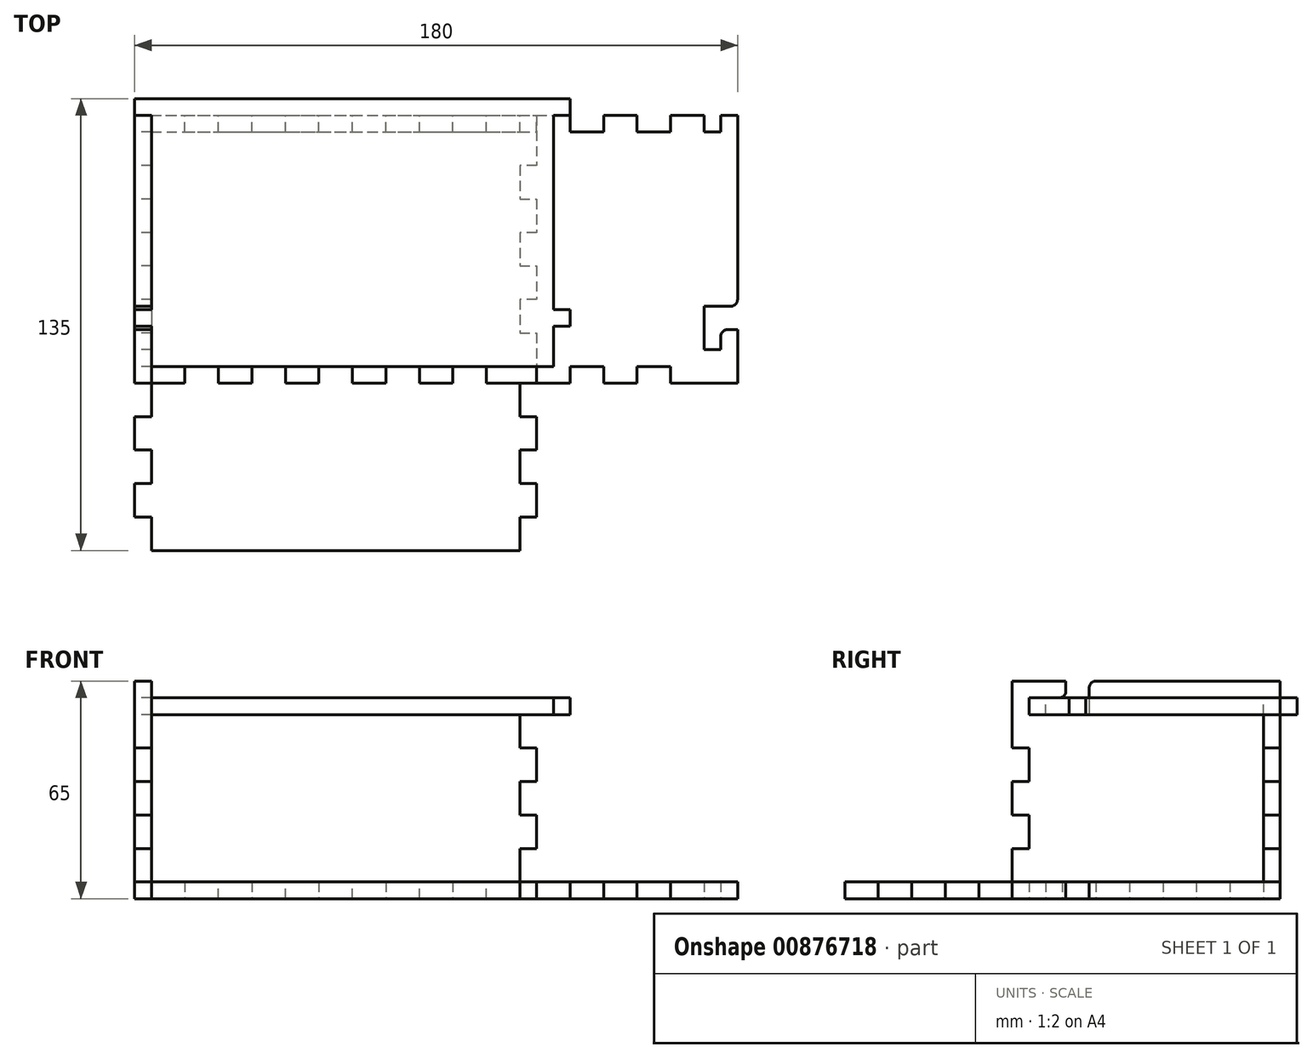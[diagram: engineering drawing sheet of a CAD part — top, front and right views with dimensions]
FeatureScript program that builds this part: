
annotation { "Feature Type Name" : "Feature", "Feature Type Description" : "" }
export const myFeature = defineFeature(function(context is Context, id is Id, definition is map)
    precondition{}
    {
        {
            assignVariable(context, id + "F0", {"name" : "thick", "anyValue" : 5});
        }
        {
            var Q0;
            Q0=qCreatedBy(makeId("Top.planeOp"),FACE);
            var sketch = newSketch(context, id + "F1", { "sketchPlane" : qUnion([Q0])});
            skLineSegment(sketch, "E0", {"start": v(0, 60.97) * mm, "end": v(0, 0) * mm, "construction": true});
            skLineSegment(sketch, "E1", {"start": v(0, 0) * mm, "end": v(112.46, 0) * mm, "construction": true});
            skPoint(sketch, "E2", {"position": v(65, 55) * mm});
            skPoint(sketch, "E3", {"position": v(65, 135) * mm});
            skPoint(sketch, "E4", {"position": v(185, 135) * mm});
            skPoint(sketch, "E5", {"position": v(185, 55) * mm});
            skLineSegment(sketch, "E6", {"start": v(65, 135) * mm, "end": v(80, 135) * mm});
            skLineSegment(sketch, "E7", {"start": v(80, 135) * mm, "end": v(80, 130) * mm});
            skLineSegment(sketch, "E8", {"start": v(80, 130) * mm, "end": v(90, 130) * mm});
            skLineSegment(sketch, "E9", {"start": v(90, 130) * mm, "end": v(90, 135) * mm});
            skLineSegment(sketch, "E10", {"start": v(90, 135) * mm, "end": v(100, 135) * mm});
            skLineSegment(sketch, "E11", {"start": v(100, 135) * mm, "end": v(100, 130) * mm});
            skLineSegment(sketch, "E12", {"start": v(100, 130) * mm, "end": v(110, 130) * mm});
            skLineSegment(sketch, "E13", {"start": v(110, 130) * mm, "end": v(110, 135) * mm});
            skLineSegment(sketch, "E14", {"start": v(110, 135) * mm, "end": v(120, 135) * mm});
            skLineSegment(sketch, "E15", {"start": v(120, 135) * mm, "end": v(120, 130) * mm});
            skLineSegment(sketch, "E16", {"start": v(120, 130) * mm, "end": v(130, 130) * mm});
            skLineSegment(sketch, "E17", {"start": v(130, 130) * mm, "end": v(130, 135) * mm});
            skLineSegment(sketch, "E18", {"start": v(130, 135) * mm, "end": v(140, 135) * mm});
            skLineSegment(sketch, "E19", {"start": v(140, 135) * mm, "end": v(140, 130) * mm});
            skLineSegment(sketch, "E20", {"start": v(140, 130) * mm, "end": v(150, 130) * mm});
            skLineSegment(sketch, "E21", {"start": v(150, 130) * mm, "end": v(150, 135) * mm});
            skLineSegment(sketch, "E22", {"start": v(150, 135) * mm, "end": v(160, 135) * mm});
            skLineSegment(sketch, "E23", {"start": v(160, 135) * mm, "end": v(160, 130) * mm});
            skLineSegment(sketch, "E24", {"start": v(160, 130) * mm, "end": v(170, 130) * mm});
            skLineSegment(sketch, "E25", {"start": v(170, 130) * mm, "end": v(170, 135) * mm});
            skLineSegment(sketch, "E26", {"start": v(170, 135) * mm, "end": v(185, 135) * mm});
            skLineSegment(sketch, "E27", {"start": v(65, 135) * mm, "end": v(65, 120) * mm});
            skLineSegment(sketch, "E28", {"start": v(65, 120) * mm, "end": v(70, 120) * mm});
            skLineSegment(sketch, "E29", {"start": v(70, 120) * mm, "end": v(70, 110) * mm});
            skLineSegment(sketch, "E30", {"start": v(70, 110) * mm, "end": v(65, 110) * mm});
            skLineSegment(sketch, "E31", {"start": v(65, 110) * mm, "end": v(65, 100) * mm});
            skLineSegment(sketch, "E32", {"start": v(65, 100) * mm, "end": v(70, 100) * mm});
            skLineSegment(sketch, "E33", {"start": v(70, 100) * mm, "end": v(70, 90) * mm});
            skLineSegment(sketch, "E34", {"start": v(70, 90) * mm, "end": v(65, 90) * mm});
            skLineSegment(sketch, "E35", {"start": v(65, 90) * mm, "end": v(65, 80) * mm});
            skLineSegment(sketch, "E36", {"start": v(65, 80) * mm, "end": v(70, 80) * mm});
            skLineSegment(sketch, "E37", {"start": v(70, 80) * mm, "end": v(70, 70) * mm});
            skLineSegment(sketch, "E38", {"start": v(70, 70) * mm, "end": v(65, 70) * mm});
            skLineSegment(sketch, "E39", {"start": v(65, 70) * mm, "end": v(65, 55) * mm});
            skPoint(sketch, "E40", {"position": v(65, 185) * mm});
            skPoint(sketch, "E41", {"position": v(15, 135) * mm});
            skLineSegment(sketch, "E42", {"start": v(70, 145) * mm, "end": v(65, 145) * mm});
            skLineSegment(sketch, "E43", {"start": v(65, 145) * mm, "end": v(65, 155) * mm});
            skLineSegment(sketch, "E44", {"start": v(65, 155) * mm, "end": v(70, 155) * mm});
            skLineSegment(sketch, "E45", {"start": v(70, 155) * mm, "end": v(70, 165) * mm});
            skLineSegment(sketch, "E46", {"start": v(70, 165) * mm, "end": v(65, 165) * mm});
            skLineSegment(sketch, "E47", {"start": v(65, 165) * mm, "end": v(65, 175) * mm});
            skLineSegment(sketch, "E48", {"start": v(65, 175) * mm, "end": v(70, 175) * mm});
            skLineSegment(sketch, "E49", {"start": v(70, 95) * mm, "end": v(111.5, 95) * mm, "construction": true});
            skLineSegment(sketch, "E50", {"start": v(70, 145) * mm, "end": v(70, 135) * mm});
            skLineSegment(sketch, "E51", {"start": v(70, 175) * mm, "end": v(70, 185) * mm});
            skLineSegment(sketch, "E52", {"start": v(125, 130) * mm, "end": v(125, 102.1) * mm, "construction": true});
            skLineSegment(sketch, "E53", {"start": v(10, 135) * mm, "end": v(5, 135) * mm});
            skLineSegment(sketch, "E54", {"start": v(5, 135) * mm, "end": v(5, 80) * mm});
            skLineSegment(sketch, "E55", {"start": v(7, 78) * mm, "end": v(15, 78) * mm});
            skLineSegment(sketch, "E56", {"start": v(15, 78) * mm, "end": v(15, 65) * mm});
            skLineSegment(sketch, "E57", {"start": v(15, 65) * mm, "end": v(10, 65) * mm});
            skLineSegment(sketch, "E58", {"start": v(10, 65) * mm, "end": v(10, 69) * mm});
            skLineSegment(sketch, "E59", {"start": v(8, 71) * mm, "end": v(5, 71) * mm});
            skLineSegment(sketch, "E60", {"start": v(5, 71) * mm, "end": v(5, 55) * mm});
            skPoint(sketch, "E61", {"position": v(65, 190) * mm});
            skPoint(sketch, "E62", {"position": v(65, 270) * mm});
            skLineSegment(sketch, "E63", {"start": v(65, 270) * mm, "end": v(60, 270) * mm});
            skLineSegment(sketch, "E64", {"start": v(60, 270) * mm, "end": v(60, 265) * mm});
            skLineSegment(sketch, "E65", {"start": v(60, 265) * mm, "end": v(65, 265) * mm});
            skLineSegment(sketch, "E66", {"start": v(65, 265) * mm, "end": v(65, 207) * mm});
            skLineSegment(sketch, "E67", {"start": v(65, 207) * mm, "end": v(60, 207) * mm});
            skLineSegment(sketch, "E68", {"start": v(60, 207) * mm, "end": v(60, 202) * mm});
            skLineSegment(sketch, "E69", {"start": v(60, 202) * mm, "end": v(65, 202) * mm});
            skLineSegment(sketch, "E70", {"start": v(65, 202) * mm, "end": v(65, 190) * mm});
            skLineSegment(sketch, "E71", {"start": v(65, 135) * mm, "end": v(55, 135) * mm});
            skLineSegment(sketch, "E72", {"start": v(55, 135) * mm, "end": v(55, 130) * mm});
            skLineSegment(sketch, "E73", {"start": v(55, 130) * mm, "end": v(45, 130) * mm});
            skLineSegment(sketch, "E74", {"start": v(45, 130) * mm, "end": v(45, 135) * mm});
            skLineSegment(sketch, "E75", {"start": v(45, 135) * mm, "end": v(35, 135) * mm});
            skLineSegment(sketch, "E76", {"start": v(35, 135) * mm, "end": v(35, 130) * mm});
            skLineSegment(sketch, "E77", {"start": v(35, 130) * mm, "end": v(25, 130) * mm});
            skLineSegment(sketch, "E78", {"start": v(25, 130) * mm, "end": v(25, 135) * mm});
            skLineSegment(sketch, "E79", {"start": v(25, 135) * mm, "end": v(15, 135) * mm});
            skLineSegment(sketch, "E80", {"start": v(15, 135) * mm, "end": v(15, 130) * mm});
            skLineSegment(sketch, "E81", {"start": v(15, 130) * mm, "end": v(10, 130) * mm});
            skLineSegment(sketch, "E82", {"start": v(10, 130) * mm, "end": v(10, 135) * mm});
            skPoint(sketch, "E83.visualSharp", {"position": v(5, 78) * mm});
            skArc(sketch, "E83.filletArc", {"start": v(5, 80) * mm, "mid": v(5.59, 78.59) * mm, "end": v(7, 78) * mm});
            skPoint(sketch, "E84.visualSharp", {"position": v(10, 71) * mm});
            skArc(sketch, "E84.filletArc", {"start": v(10, 69) * mm, "mid": v(9.41, 70.41) * mm, "end": v(8, 71) * mm});
            skLineSegment(sketch, "E85.MirrorCS", {"start": v(190, 207) * mm, "end": v(190, 202) * mm});
            skLineSegment(sketch, "E86.MirrorCS", {"start": v(185, 270) * mm, "end": v(190, 270) * mm});
            skLineSegment(sketch, "E87.MirrorCS", {"start": v(185, 175) * mm, "end": v(180, 175) * mm});
            skLineSegment(sketch, "E88.MirrorCS", {"start": v(190, 270) * mm, "end": v(190, 265) * mm});
            skLineSegment(sketch, "E89.MirrorCS", {"start": v(180, 165) * mm, "end": v(185, 165) * mm});
            skLineSegment(sketch, "E90.MirrorCS", {"start": v(185, 207) * mm, "end": v(190, 207) * mm});
            skLineSegment(sketch, "E91.MirrorCS", {"start": v(180, 145) * mm, "end": v(185, 145) * mm});
            skLineSegment(sketch, "E92.MirrorCS", {"start": v(190, 265) * mm, "end": v(185, 265) * mm});
            skLineSegment(sketch, "E93.MirrorCS", {"start": v(185, 155) * mm, "end": v(180, 155) * mm});
            skLineSegment(sketch, "E94.MirrorCS", {"start": v(185, 165) * mm, "end": v(185, 175) * mm});
            skLineSegment(sketch, "E95.MirrorCS", {"start": v(190, 202) * mm, "end": v(185, 202) * mm});
            skPoint(sketch, "E96.MirrorP", {"position": v(185, 270) * mm});
            skLineSegment(sketch, "E97.MirrorCS", {"start": v(185, 265) * mm, "end": v(185, 207) * mm});
            skLineSegment(sketch, "E98.MirrorCS", {"start": v(180, 155) * mm, "end": v(180, 165) * mm});
            skPoint(sketch, "E99.MirrorP", {"position": v(185, 190) * mm});
            skLineSegment(sketch, "E100.MirrorCS", {"start": v(180, 175) * mm, "end": v(180, 185) * mm});
            skLineSegment(sketch, "E101.MirrorCS", {"start": v(185, 202) * mm, "end": v(185, 190) * mm});
            skPoint(sketch, "E102.MirrorP", {"position": v(185, 185) * mm});
            skLineSegment(sketch, "E103.MirrorCS", {"start": v(185, 145) * mm, "end": v(185, 155) * mm});
            skLineSegment(sketch, "E104.MirrorCS", {"start": v(180, 145) * mm, "end": v(180, 135) * mm});
            skLineSegment(sketch, "E105.MirrorCS", {"start": v(185, 120) * mm, "end": v(180, 120) * mm});
            skLineSegment(sketch, "E106.MirrorCS", {"start": v(180, 110) * mm, "end": v(185, 110) * mm});
            skLineSegment(sketch, "E107.MirrorCS", {"start": v(185, 100) * mm, "end": v(180, 100) * mm});
            skLineSegment(sketch, "E108.MirrorCS", {"start": v(180, 70) * mm, "end": v(185, 70) * mm});
            skLineSegment(sketch, "E109.MirrorCS", {"start": v(180, 90) * mm, "end": v(185, 90) * mm});
            skLineSegment(sketch, "E110.MirrorCS", {"start": v(185, 80) * mm, "end": v(180, 80) * mm});
            skLineSegment(sketch, "E111.MirrorCS", {"start": v(180, 100) * mm, "end": v(180, 90) * mm});
            skLineSegment(sketch, "E112.MirrorCS", {"start": v(185, 135) * mm, "end": v(185, 120) * mm});
            skLineSegment(sketch, "E113.MirrorCS", {"start": v(180, 95) * mm, "end": v(138.5, 95) * mm, "construction": true});
            skLineSegment(sketch, "E114.MirrorCS", {"start": v(185, 90) * mm, "end": v(185, 80) * mm});
            skLineSegment(sketch, "E115.MirrorCS", {"start": v(180, 120) * mm, "end": v(180, 110) * mm});
            skLineSegment(sketch, "E116.MirrorCS", {"start": v(185, 70) * mm, "end": v(185, 55) * mm});
            skLineSegment(sketch, "E117.MirrorCS", {"start": v(180, 80) * mm, "end": v(180, 70) * mm});
            skLineSegment(sketch, "E118.MirrorCS", {"start": v(185, 110) * mm, "end": v(185, 100) * mm});
            skLineSegment(sketch, "E119.MirrorCS", {"start": v(242, 71) * mm, "end": v(245, 71) * mm});
            skArc(sketch, "E120.MirrorCS", {"start": v(240, 69) * mm, "mid": v(240.59, 70.41) * mm, "end": v(242, 71) * mm});
            skArc(sketch, "E121.MirrorCS", {"start": v(245, 80) * mm, "mid": v(244.41, 78.59) * mm, "end": v(243, 78) * mm});
            skLineSegment(sketch, "E122.MirrorCS", {"start": v(235, 130) * mm, "end": v(240, 130) * mm});
            skLineSegment(sketch, "E123.MirrorCS", {"start": v(215, 135) * mm, "end": v(215, 130) * mm});
            skLineSegment(sketch, "E124.MirrorCS", {"start": v(225, 130) * mm, "end": v(225, 135) * mm});
            skLineSegment(sketch, "E125.MirrorCS", {"start": v(240, 65) * mm, "end": v(240, 69) * mm});
            skLineSegment(sketch, "E126.MirrorCS", {"start": v(235, 65) * mm, "end": v(240, 65) * mm});
            skLineSegment(sketch, "E127.MirrorCS", {"start": v(195, 135) * mm, "end": v(195, 130) * mm});
            skLineSegment(sketch, "E128.MirrorCS", {"start": v(235, 135) * mm, "end": v(235, 130) * mm});
            skLineSegment(sketch, "E129.MirrorCS", {"start": v(240, 130) * mm, "end": v(240, 135) * mm});
            skLineSegment(sketch, "E130.MirrorCS", {"start": v(205, 130) * mm, "end": v(205, 135) * mm});
            skLineSegment(sketch, "E131.MirrorCS", {"start": v(240, 135) * mm, "end": v(245, 135) * mm});
            skLineSegment(sketch, "E132.MirrorCS", {"start": v(243, 78) * mm, "end": v(235, 78) * mm});
            skLineSegment(sketch, "E133.MirrorCS", {"start": v(205, 135) * mm, "end": v(215, 135) * mm});
            skLineSegment(sketch, "E134.MirrorCS", {"start": v(245, 135) * mm, "end": v(245, 80) * mm});
            skLineSegment(sketch, "E135.MirrorCS", {"start": v(215, 130) * mm, "end": v(225, 130) * mm});
            skLineSegment(sketch, "E136.MirrorCS", {"start": v(195, 130) * mm, "end": v(205, 130) * mm});
            skLineSegment(sketch, "E137.MirrorCS", {"start": v(225, 135) * mm, "end": v(235, 135) * mm});
            skPoint(sketch, "E138.MirrorP", {"position": v(245, 78) * mm});
            skPoint(sketch, "E139.MirrorP", {"position": v(235, 135) * mm});
            skLineSegment(sketch, "E140.MirrorCS", {"start": v(235, 78) * mm, "end": v(235, 65) * mm});
            skLineSegment(sketch, "E141.MirrorCS", {"start": v(245, 71) * mm, "end": v(245, 55) * mm});
            skPoint(sketch, "E142.MirrorP", {"position": v(240, 71) * mm});
            skLineSegment(sketch, "E143.MirrorCS", {"start": v(185, 135) * mm, "end": v(195, 135) * mm});
            skLineSegment(sketch, "E144", {"start": v(70, 185) * mm, "end": v(180, 185) * mm});
            skLineSegment(sketch, "E145", {"start": v(65, 190) * mm, "end": v(185, 190) * mm});
            skLineSegment(sketch, "E146", {"start": v(65, 270) * mm, "end": v(185, 270) * mm});
            skLineSegment(sketch, "E147.MirrorCS", {"start": v(150, 60) * mm, "end": v(150, 55) * mm});
            skLineSegment(sketch, "E148.MirrorCS", {"start": v(170, 60) * mm, "end": v(170, 55) * mm});
            skLineSegment(sketch, "E149.MirrorCS", {"start": v(65, 35) * mm, "end": v(70, 35) * mm});
            skLineSegment(sketch, "E150.MirrorCS", {"start": v(130, 60) * mm, "end": v(130, 55) * mm});
            skLineSegment(sketch, "E151.MirrorCS", {"start": v(140, 55) * mm, "end": v(140, 60) * mm});
            skLineSegment(sketch, "E152.MirrorCS", {"start": v(65, 15) * mm, "end": v(70, 15) * mm});
            skLineSegment(sketch, "E153.MirrorCS", {"start": v(110, 60) * mm, "end": v(110, 55) * mm});
            skLineSegment(sketch, "E154.MirrorCS", {"start": v(120, 55) * mm, "end": v(120, 60) * mm});
            skLineSegment(sketch, "E155.MirrorCS", {"start": v(180, 25) * mm, "end": v(185, 25) * mm});
            skLineSegment(sketch, "E156.MirrorCS", {"start": v(185, 15) * mm, "end": v(180, 15) * mm});
            skLineSegment(sketch, "E157.MirrorCS", {"start": v(70, 25) * mm, "end": v(65, 25) * mm});
            skLineSegment(sketch, "E158.MirrorCS", {"start": v(100, 55) * mm, "end": v(100, 60) * mm});
            skLineSegment(sketch, "E159.MirrorCS", {"start": v(90, 60) * mm, "end": v(90, 55) * mm});
            skLineSegment(sketch, "E160.MirrorCS", {"start": v(185, 35) * mm, "end": v(180, 35) * mm});
            skLineSegment(sketch, "E161.MirrorCS", {"start": v(160, 55) * mm, "end": v(160, 60) * mm});
            skLineSegment(sketch, "E162.MirrorCS", {"start": v(80, 55) * mm, "end": v(80, 60) * mm});
            skLineSegment(sketch, "E163.MirrorCS", {"start": v(70, 45) * mm, "end": v(65, 45) * mm});
            skLineSegment(sketch, "E164.MirrorCS", {"start": v(180, 45) * mm, "end": v(185, 45) * mm});
            skLineSegment(sketch, "E165.MirrorCS", {"start": v(120, 60) * mm, "end": v(130, 60) * mm});
            skPoint(sketch, "E166.MirrorP", {"position": v(185, 5) * mm});
            skLineSegment(sketch, "E167.MirrorCS", {"start": v(65, 55) * mm, "end": v(80, 55) * mm});
            skLineSegment(sketch, "E168.MirrorCS", {"start": v(70, 35) * mm, "end": v(70, 25) * mm});
            skLineSegment(sketch, "E169.MirrorCS", {"start": v(185, 25) * mm, "end": v(185, 15) * mm});
            skLineSegment(sketch, "E170.MirrorCS", {"start": v(70, 5) * mm, "end": v(180, 5) * mm});
            skLineSegment(sketch, "E171.MirrorCS", {"start": v(180, 15) * mm, "end": v(180, 5) * mm});
            skLineSegment(sketch, "E172.MirrorCS", {"start": v(160, 60) * mm, "end": v(170, 60) * mm});
            skLineSegment(sketch, "E173.MirrorCS", {"start": v(65, 25) * mm, "end": v(65, 15) * mm});
            skLineSegment(sketch, "E174.MirrorCS", {"start": v(70, 15) * mm, "end": v(70, 5) * mm});
            skLineSegment(sketch, "E175.MirrorCS", {"start": v(180, 45) * mm, "end": v(180, 55) * mm});
            skLineSegment(sketch, "E176.MirrorCS", {"start": v(170, 55) * mm, "end": v(185, 55) * mm});
            skLineSegment(sketch, "E177.MirrorCS", {"start": v(185, 45) * mm, "end": v(185, 35) * mm});
            skPoint(sketch, "E178.MirrorP", {"position": v(65, 5) * mm});
            skLineSegment(sketch, "E179.MirrorCS", {"start": v(110, 55) * mm, "end": v(120, 55) * mm});
            skLineSegment(sketch, "E180.MirrorCS", {"start": v(140, 60) * mm, "end": v(150, 60) * mm});
            skLineSegment(sketch, "E181.MirrorCS", {"start": v(100, 60) * mm, "end": v(110, 60) * mm});
            skLineSegment(sketch, "E182.MirrorCS", {"start": v(180, 35) * mm, "end": v(180, 25) * mm});
            skLineSegment(sketch, "E183.MirrorCS", {"start": v(150, 55) * mm, "end": v(160, 55) * mm});
            skLineSegment(sketch, "E184.MirrorCS", {"start": v(90, 55) * mm, "end": v(100, 55) * mm});
            skLineSegment(sketch, "E185.MirrorCS", {"start": v(80, 60) * mm, "end": v(90, 60) * mm});
            skLineSegment(sketch, "E186.MirrorCS", {"start": v(65, 45) * mm, "end": v(65, 35) * mm});
            skLineSegment(sketch, "E187.MirrorCS", {"start": v(70, 45) * mm, "end": v(70, 55) * mm});
            skLineSegment(sketch, "E188.MirrorCS", {"start": v(130, 55) * mm, "end": v(140, 55) * mm});
            skLineSegment(sketch, "E189.MirrorCS", {"start": v(45, 60) * mm, "end": v(45, 55) * mm});
            skLineSegment(sketch, "E190.MirrorCS", {"start": v(55, 60) * mm, "end": v(45, 60) * mm});
            skLineSegment(sketch, "E191.MirrorCS", {"start": v(45, 55) * mm, "end": v(35, 55) * mm});
            skLineSegment(sketch, "E192.MirrorCS", {"start": v(55, 55) * mm, "end": v(55, 60) * mm});
            skLineSegment(sketch, "E193.MirrorCS", {"start": v(35, 60) * mm, "end": v(25, 60) * mm});
            skLineSegment(sketch, "E194.MirrorCS", {"start": v(25, 60) * mm, "end": v(25, 55) * mm});
            skLineSegment(sketch, "E195.MirrorCS", {"start": v(65, 55) * mm, "end": v(55, 55) * mm});
            skLineSegment(sketch, "E196.MirrorCS", {"start": v(35, 55) * mm, "end": v(35, 60) * mm});
            skLineSegment(sketch, "E197.MirrorCS", {"start": v(25, 55) * mm, "end": v(15, 55) * mm});
            skLineSegment(sketch, "E198.MirrorCS", {"start": v(205, 55) * mm, "end": v(215, 55) * mm});
            skLineSegment(sketch, "E199.MirrorCS", {"start": v(205, 60) * mm, "end": v(205, 55) * mm});
            skLineSegment(sketch, "E200.MirrorCS", {"start": v(225, 55) * mm, "end": v(235, 55) * mm});
            skLineSegment(sketch, "E201.MirrorCS", {"start": v(185, 55) * mm, "end": v(195, 55) * mm});
            skLineSegment(sketch, "E202.MirrorCS", {"start": v(215, 55) * mm, "end": v(215, 60) * mm});
            skLineSegment(sketch, "E203.MirrorCS", {"start": v(225, 60) * mm, "end": v(225, 55) * mm});
            skLineSegment(sketch, "E204.MirrorCS", {"start": v(195, 60) * mm, "end": v(205, 60) * mm});
            skLineSegment(sketch, "E205.MirrorCS", {"start": v(195, 55) * mm, "end": v(195, 60) * mm});
            skLineSegment(sketch, "E206.MirrorCS", {"start": v(215, 60) * mm, "end": v(225, 60) * mm});
            skLineSegment(sketch, "E207", {"start": v(15, 55) * mm, "end": v(5, 55) * mm});
            skLineSegment(sketch, "E208", {"start": v(235, 55) * mm, "end": v(245, 55) * mm});
            skSolve(sketch);
        }
        {
            var Q0;
            {var subQ6=sQuery(id+"F1.wireOp",EDGE,"E7");Q0=makeQuery(id+"F1.imprint","IMPRINT",FACE,{"disambiguationData":[TD([[makeQuery(id+"F1.imprint","IMPRINT",EDGE,{"derivedFrom":subQ6}),-1.0]])]});}
            extrude(context, id + "F2", {"entities" : qUnion([Q0]), "depth" : (getVariable(context, 'thick')) * mm, "offsetDistance" : 25 * mm});
        }
        {
            var Q0;
            {var subQ3=sQuery(id+"F1.wireOp",EDGE,"E7");Q0=makeQuery(id+"F1.imprint","IMPRINT",FACE,{"disambiguationData":[TD([[makeQuery(id+"F1.imprint","IMPRINT",EDGE,{"derivedFrom":subQ3}),1.0]])]});}
            var Q1;
            Q1=makeQuery(id+"F1.imprint","IMPRINT",FACE,{"disambiguationData":[TD([[makeQuery(id+"F1.imprint","IMPRINT",EDGE,{"derivedFrom":sQuery(id+"F1.wireOp",EDGE,"E27")}),-1.0]])]});
            var Q2;
            Q2=makeQuery(id+"F1.imprint","IMPRINT",FACE,{"disambiguationData":[TD([[makeQuery(id+"F1.imprint","IMPRINT",EDGE,{"derivedFrom":sQuery(id+"F1.wireOp",EDGE,"E147.MirrorCS")}),-1.0]])]});
            var Q3;
            Q3=makeQuery(id+"F1.imprint","IMPRINT",FACE,{"disambiguationData":[TD([[makeQuery(id+"F1.imprint","IMPRINT",EDGE,{"derivedFrom":sQuery(id+"F1.wireOp",EDGE,"E105.MirrorCS")}),1.0]])]});
            var Q4;
            Q4=makeQuery(id+"F1.imprint","IMPRINT",FACE,{"disambiguationData":[TD([[makeQuery(id+"F1.imprint","IMPRINT",EDGE,{"derivedFrom":sQuery(id+"F1.wireOp",EDGE,"E63")}),1.0]])]});
            extrude(context, id + "F3", {"entities" : qUnion([Q0, Q1, Q2, Q3, Q4]), "depth" : (getVariable(context, 'thick')) * mm, "offsetDistance" : 25 * mm});
        }
        {
            var Q0;
            Q0=makeQuery(id+"F3.opExtrude","SWEPT_BODY",BODY,{"disambiguationData":[OSD([sQuery(id+"F1.wireOp",EDGE,"E6"),sQuery(id+"F1.wireOp",EDGE,"E7"),sQuery(id+"F1.wireOp",EDGE,"E8"),sQuery(id+"F1.wireOp",EDGE,"E9"),sQuery(id+"F1.wireOp",EDGE,"E10"),sQuery(id+"F1.wireOp",EDGE,"E11"),sQuery(id+"F1.wireOp",EDGE,"E12"),sQuery(id+"F1.wireOp",EDGE,"E13"),sQuery(id+"F1.wireOp",EDGE,"E14"),sQuery(id+"F1.wireOp",EDGE,"E15"),sQuery(id+"F1.wireOp",EDGE,"E16"),sQuery(id+"F1.wireOp",EDGE,"E17"),sQuery(id+"F1.wireOp",EDGE,"E18"),sQuery(id+"F1.wireOp",EDGE,"E19"),sQuery(id+"F1.wireOp",EDGE,"E20"),sQuery(id+"F1.wireOp",EDGE,"E21"),sQuery(id+"F1.wireOp",EDGE,"E22"),sQuery(id+"F1.wireOp",EDGE,"E23"),sQuery(id+"F1.wireOp",EDGE,"E24"),sQuery(id+"F1.wireOp",EDGE,"E25"),sQuery(id+"F1.wireOp",EDGE,"E26"),sQuery(id+"F1.wireOp",EDGE,"E42"),sQuery(id+"F1.wireOp",EDGE,"E43"),sQuery(id+"F1.wireOp",EDGE,"E44"),sQuery(id+"F1.wireOp",EDGE,"E45"),sQuery(id+"F1.wireOp",EDGE,"E46"),sQuery(id+"F1.wireOp",EDGE,"E47"),sQuery(id+"F1.wireOp",EDGE,"E48"),sQuery(id+"F1.wireOp",EDGE,"E50"),sQuery(id+"F1.wireOp",EDGE,"E51"),sQuery(id+"F1.wireOp",EDGE,"E87.MirrorCS"),sQuery(id+"F1.wireOp",EDGE,"E89.MirrorCS"),sQuery(id+"F1.wireOp",EDGE,"E91.MirrorCS"),sQuery(id+"F1.wireOp",EDGE,"E93.MirrorCS"),sQuery(id+"F1.wireOp",EDGE,"E94.MirrorCS"),sQuery(id+"F1.wireOp",EDGE,"E98.MirrorCS"),sQuery(id+"F1.wireOp",EDGE,"E100.MirrorCS"),sQuery(id+"F1.wireOp",EDGE,"E103.MirrorCS"),sQuery(id+"F1.wireOp",EDGE,"E104.MirrorCS"),sQuery(id+"F1.wireOp",EDGE,"E144")])]});
            var Q1;
            Q1=makeQuery(id+"F3.opExtrude","CAP_EDGE",EDGE,{"disambiguationData":[OSD([sQuery(id+"F1.wireOp",EDGE,"E6")])],"isStart":false});
            transform(context, id + "F4", {"entities" : qUnion([Q0]), "transformType" : TransformType.ROTATION, "transformAxis" : qUnion([Q1]), "angle" : 90 * degree, "makeCopy" : false});
        }
        {
            var Q0;
            Q0=makeQuery(id+"F3.opExtrude","SWEPT_BODY",BODY,{"disambiguationData":[OSD([sQuery(id+"F1.wireOp",EDGE,"E6"),sQuery(id+"F1.wireOp",EDGE,"E7"),sQuery(id+"F1.wireOp",EDGE,"E8"),sQuery(id+"F1.wireOp",EDGE,"E9"),sQuery(id+"F1.wireOp",EDGE,"E10"),sQuery(id+"F1.wireOp",EDGE,"E11"),sQuery(id+"F1.wireOp",EDGE,"E12"),sQuery(id+"F1.wireOp",EDGE,"E13"),sQuery(id+"F1.wireOp",EDGE,"E14"),sQuery(id+"F1.wireOp",EDGE,"E15"),sQuery(id+"F1.wireOp",EDGE,"E16"),sQuery(id+"F1.wireOp",EDGE,"E17"),sQuery(id+"F1.wireOp",EDGE,"E18"),sQuery(id+"F1.wireOp",EDGE,"E19"),sQuery(id+"F1.wireOp",EDGE,"E20"),sQuery(id+"F1.wireOp",EDGE,"E21"),sQuery(id+"F1.wireOp",EDGE,"E22"),sQuery(id+"F1.wireOp",EDGE,"E23"),sQuery(id+"F1.wireOp",EDGE,"E24"),sQuery(id+"F1.wireOp",EDGE,"E25"),sQuery(id+"F1.wireOp",EDGE,"E26"),sQuery(id+"F1.wireOp",EDGE,"E42"),sQuery(id+"F1.wireOp",EDGE,"E43"),sQuery(id+"F1.wireOp",EDGE,"E44"),sQuery(id+"F1.wireOp",EDGE,"E45"),sQuery(id+"F1.wireOp",EDGE,"E46"),sQuery(id+"F1.wireOp",EDGE,"E47"),sQuery(id+"F1.wireOp",EDGE,"E48"),sQuery(id+"F1.wireOp",EDGE,"E50"),sQuery(id+"F1.wireOp",EDGE,"E51"),sQuery(id+"F1.wireOp",EDGE,"E87.MirrorCS"),sQuery(id+"F1.wireOp",EDGE,"E89.MirrorCS"),sQuery(id+"F1.wireOp",EDGE,"E91.MirrorCS"),sQuery(id+"F1.wireOp",EDGE,"E93.MirrorCS"),sQuery(id+"F1.wireOp",EDGE,"E94.MirrorCS"),sQuery(id+"F1.wireOp",EDGE,"E98.MirrorCS"),sQuery(id+"F1.wireOp",EDGE,"E100.MirrorCS"),sQuery(id+"F1.wireOp",EDGE,"E103.MirrorCS"),sQuery(id+"F1.wireOp",EDGE,"E104.MirrorCS"),sQuery(id+"F1.wireOp",EDGE,"E144")])]});
            var Q1;
            Q1=makeQuery(id+"F3.opExtrude","SWEPT_EDGE",EDGE,{"disambiguationData":[OSD([sQuery(id+"F1.wireOp",EDGE,"E6"),sQuery(id+"F1.wireOp",EDGE,"E50")])]});
            transform(context, id + "F5", {"entities" : qUnion([Q0]), "transformType" : TransformType.TRANSLATION_ENTITY, "oppositeDirectionEntity" : true, "transformLine" : qUnion([Q1]), "makeCopy" : false});
        }
        {
            var Q0;
            Q0=makeQuery(id+"F3.opExtrude","SWEPT_BODY",BODY,{"disambiguationData":[OSD([sQuery(id+"F1.wireOp",EDGE,"E27"),sQuery(id+"F1.wireOp",EDGE,"E28"),sQuery(id+"F1.wireOp",EDGE,"E29"),sQuery(id+"F1.wireOp",EDGE,"E30"),sQuery(id+"F1.wireOp",EDGE,"E31"),sQuery(id+"F1.wireOp",EDGE,"E32"),sQuery(id+"F1.wireOp",EDGE,"E33"),sQuery(id+"F1.wireOp",EDGE,"E34"),sQuery(id+"F1.wireOp",EDGE,"E35"),sQuery(id+"F1.wireOp",EDGE,"E36"),sQuery(id+"F1.wireOp",EDGE,"E37"),sQuery(id+"F1.wireOp",EDGE,"E38"),sQuery(id+"F1.wireOp",EDGE,"E39"),sQuery(id+"F1.wireOp",EDGE,"E53"),sQuery(id+"F1.wireOp",EDGE,"E54"),sQuery(id+"F1.wireOp",EDGE,"E55"),sQuery(id+"F1.wireOp",EDGE,"E56"),sQuery(id+"F1.wireOp",EDGE,"E57"),sQuery(id+"F1.wireOp",EDGE,"E58"),sQuery(id+"F1.wireOp",EDGE,"E59"),sQuery(id+"F1.wireOp",EDGE,"E60"),sQuery(id+"F1.wireOp",EDGE,"E71"),sQuery(id+"F1.wireOp",EDGE,"E72"),sQuery(id+"F1.wireOp",EDGE,"E73"),sQuery(id+"F1.wireOp",EDGE,"E74"),sQuery(id+"F1.wireOp",EDGE,"E75"),sQuery(id+"F1.wireOp",EDGE,"E76"),sQuery(id+"F1.wireOp",EDGE,"E77"),sQuery(id+"F1.wireOp",EDGE,"E78"),sQuery(id+"F1.wireOp",EDGE,"E79"),sQuery(id+"F1.wireOp",EDGE,"E80"),sQuery(id+"F1.wireOp",EDGE,"E81"),sQuery(id+"F1.wireOp",EDGE,"E82"),sQuery(id+"F1.wireOp",EDGE,"E83.filletArc"),sQuery(id+"F1.wireOp",EDGE,"E84.filletArc"),sQuery(id+"F1.wireOp",EDGE,"E189.MirrorCS"),sQuery(id+"F1.wireOp",EDGE,"E190.MirrorCS"),sQuery(id+"F1.wireOp",EDGE,"E191.MirrorCS"),sQuery(id+"F1.wireOp",EDGE,"E192.MirrorCS"),sQuery(id+"F1.wireOp",EDGE,"E193.MirrorCS"),sQuery(id+"F1.wireOp",EDGE,"E194.MirrorCS"),sQuery(id+"F1.wireOp",EDGE,"E195.MirrorCS"),sQuery(id+"F1.wireOp",EDGE,"E196.MirrorCS"),sQuery(id+"F1.wireOp",EDGE,"E197.MirrorCS"),sQuery(id+"F1.wireOp",EDGE,"E207")])]});
            var Q1;
            Q1=makeQuery(id+"F2.opExtrude","CAP_EDGE",EDGE,{"disambiguationData":[OSD([sQuery(id+"F1.wireOp",EDGE,"E39")])],"isStart":false});
            transform(context, id + "F6", {"entities" : qUnion([Q0]), "transformType" : TransformType.ROTATION, "transformAxis" : qUnion([Q1]), "angle" : 90 * degree, "oppositeDirection" : true, "makeCopy" : false});
        }
        {
            var Q0;
            Q0=makeQuery(id+"F3.opExtrude","SWEPT_BODY",BODY,{"disambiguationData":[OSD([sQuery(id+"F1.wireOp",EDGE,"E27"),sQuery(id+"F1.wireOp",EDGE,"E28"),sQuery(id+"F1.wireOp",EDGE,"E29"),sQuery(id+"F1.wireOp",EDGE,"E30"),sQuery(id+"F1.wireOp",EDGE,"E31"),sQuery(id+"F1.wireOp",EDGE,"E32"),sQuery(id+"F1.wireOp",EDGE,"E33"),sQuery(id+"F1.wireOp",EDGE,"E34"),sQuery(id+"F1.wireOp",EDGE,"E35"),sQuery(id+"F1.wireOp",EDGE,"E36"),sQuery(id+"F1.wireOp",EDGE,"E37"),sQuery(id+"F1.wireOp",EDGE,"E38"),sQuery(id+"F1.wireOp",EDGE,"E39"),sQuery(id+"F1.wireOp",EDGE,"E53"),sQuery(id+"F1.wireOp",EDGE,"E54"),sQuery(id+"F1.wireOp",EDGE,"E55"),sQuery(id+"F1.wireOp",EDGE,"E56"),sQuery(id+"F1.wireOp",EDGE,"E57"),sQuery(id+"F1.wireOp",EDGE,"E58"),sQuery(id+"F1.wireOp",EDGE,"E59"),sQuery(id+"F1.wireOp",EDGE,"E60"),sQuery(id+"F1.wireOp",EDGE,"E71"),sQuery(id+"F1.wireOp",EDGE,"E72"),sQuery(id+"F1.wireOp",EDGE,"E73"),sQuery(id+"F1.wireOp",EDGE,"E74"),sQuery(id+"F1.wireOp",EDGE,"E75"),sQuery(id+"F1.wireOp",EDGE,"E76"),sQuery(id+"F1.wireOp",EDGE,"E77"),sQuery(id+"F1.wireOp",EDGE,"E78"),sQuery(id+"F1.wireOp",EDGE,"E79"),sQuery(id+"F1.wireOp",EDGE,"E80"),sQuery(id+"F1.wireOp",EDGE,"E81"),sQuery(id+"F1.wireOp",EDGE,"E82"),sQuery(id+"F1.wireOp",EDGE,"E83.filletArc"),sQuery(id+"F1.wireOp",EDGE,"E84.filletArc"),sQuery(id+"F1.wireOp",EDGE,"E189.MirrorCS"),sQuery(id+"F1.wireOp",EDGE,"E190.MirrorCS"),sQuery(id+"F1.wireOp",EDGE,"E191.MirrorCS"),sQuery(id+"F1.wireOp",EDGE,"E192.MirrorCS"),sQuery(id+"F1.wireOp",EDGE,"E193.MirrorCS"),sQuery(id+"F1.wireOp",EDGE,"E194.MirrorCS"),sQuery(id+"F1.wireOp",EDGE,"E195.MirrorCS"),sQuery(id+"F1.wireOp",EDGE,"E196.MirrorCS"),sQuery(id+"F1.wireOp",EDGE,"E197.MirrorCS"),sQuery(id+"F1.wireOp",EDGE,"E207")])]});
            var Q1;
            Q1=makeQuery(id+"F3.opExtrude","SWEPT_EDGE",EDGE,{"disambiguationData":[OSD([sQuery(id+"F1.wireOp",EDGE,"E39"),sQuery(id+"F1.wireOp",EDGE,"E167.MirrorCS"),sQuery(id+"F1.wireOp",EDGE,"E195.MirrorCS")])]});
            transform(context, id + "F7", {"entities" : qUnion([Q0]), "transformType" : TransformType.TRANSLATION_ENTITY, "oppositeDirectionEntity" : true, "transformLine" : qUnion([Q1]), "makeCopy" : false});
        }
        {
            var Q0;
            Q0=makeQuery(id+"F3.opExtrude","SWEPT_BODY",BODY,{"disambiguationData":[OSD([sQuery(id+"F1.wireOp",EDGE,"E63"),sQuery(id+"F1.wireOp",EDGE,"E64"),sQuery(id+"F1.wireOp",EDGE,"E65"),sQuery(id+"F1.wireOp",EDGE,"E66"),sQuery(id+"F1.wireOp",EDGE,"E67"),sQuery(id+"F1.wireOp",EDGE,"E68"),sQuery(id+"F1.wireOp",EDGE,"E69"),sQuery(id+"F1.wireOp",EDGE,"E70"),sQuery(id+"F1.wireOp",EDGE,"E85.MirrorCS"),sQuery(id+"F1.wireOp",EDGE,"E86.MirrorCS"),sQuery(id+"F1.wireOp",EDGE,"E88.MirrorCS"),sQuery(id+"F1.wireOp",EDGE,"E90.MirrorCS"),sQuery(id+"F1.wireOp",EDGE,"E92.MirrorCS"),sQuery(id+"F1.wireOp",EDGE,"E95.MirrorCS"),sQuery(id+"F1.wireOp",EDGE,"E97.MirrorCS"),sQuery(id+"F1.wireOp",EDGE,"E101.MirrorCS"),sQuery(id+"F1.wireOp",EDGE,"E145"),sQuery(id+"F1.wireOp",EDGE,"E146")])]});
            var Q1;
            Q1=makeQuery(id+"F3.opExtrude","CAP_VERTEX",VERTEX,{"disambiguationData":[OSD([sQuery(id+"F1.wireOp",EDGE,"E64"),sQuery(id+"F1.wireOp",EDGE,"E65")])],"isStart":true});
            var Q2;
            Q2=makeQuery(id+"F3.opExtrude","CAP_VERTEX",VERTEX,{"disambiguationData":[OSD([sQuery(id+"F1.wireOp",EDGE,"E79"),sQuery(id+"F1.wireOp",EDGE,"E80")])],"isStart":true});
            transform(context, id + "F8", {"entities" : qUnion([Q0]), "transformType" : TransformType.TRANSLATION_ENTITY, "oppositeDirectionEntity" : false, "transformLine" : qUnion([Q1, Q2]), "makeCopy" : false});
        }
    });
